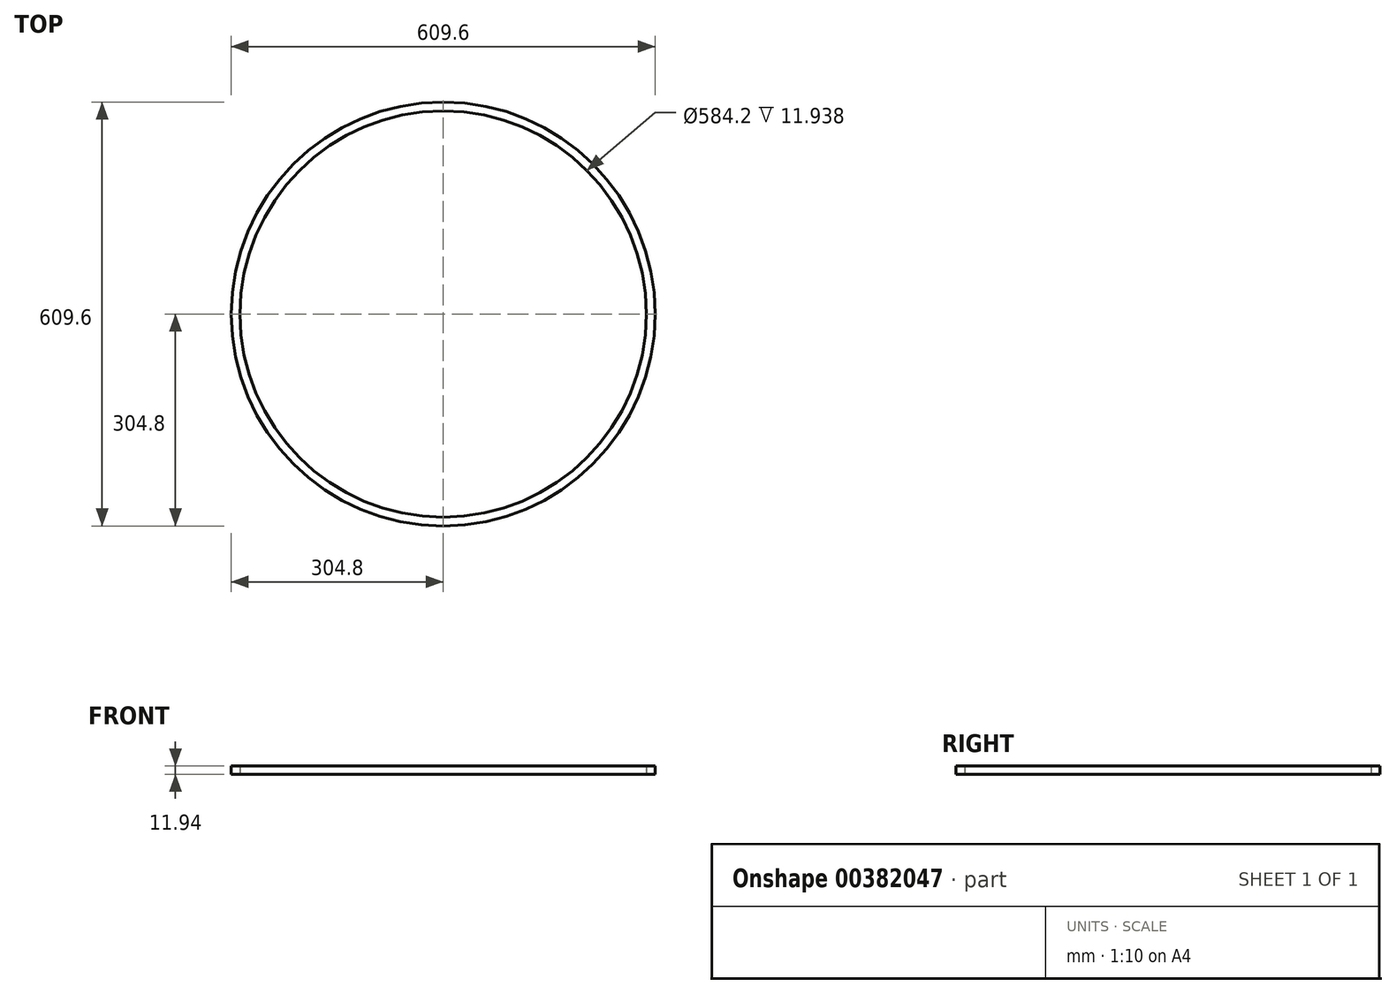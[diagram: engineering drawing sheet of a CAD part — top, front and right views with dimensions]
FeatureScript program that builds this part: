
annotation { "Feature Type Name" : "Feature", "Feature Type Description" : "" }
export const myFeature = defineFeature(function(context is Context, id is Id, definition is map)
    precondition{}
    {
        {
            var Q0;
            Q0=qCreatedBy(makeId("Top.planeOp"),FACE);
            var sketch = newSketch(context, id + "F0", { "sketchPlane" : qUnion([Q0])});
            skCircle(sketch, "E0", {"center": v(0, 0) * mm, "radius": 304.8 * mm});
            skCircle(sketch, "E1", {"center": v(0, 0) * mm, "radius": 292.1 * mm});
            skSolve(sketch);
        }
        {
            var Q0;
            Q0=makeQuery(id+"F0.imprint","IMPRINT",FACE,{"disambiguationData":[TD([[makeQuery(id+"F0.imprint","IMPRINT",EDGE,{"derivedFrom":sQuery(id+"F0.wireOp",EDGE,"E0")}),1.0]])]});
            extrude(context, id + "F1", {"entities" : qUnion([Q0]), "depth" : 11.94 * mm});
        }
    });
